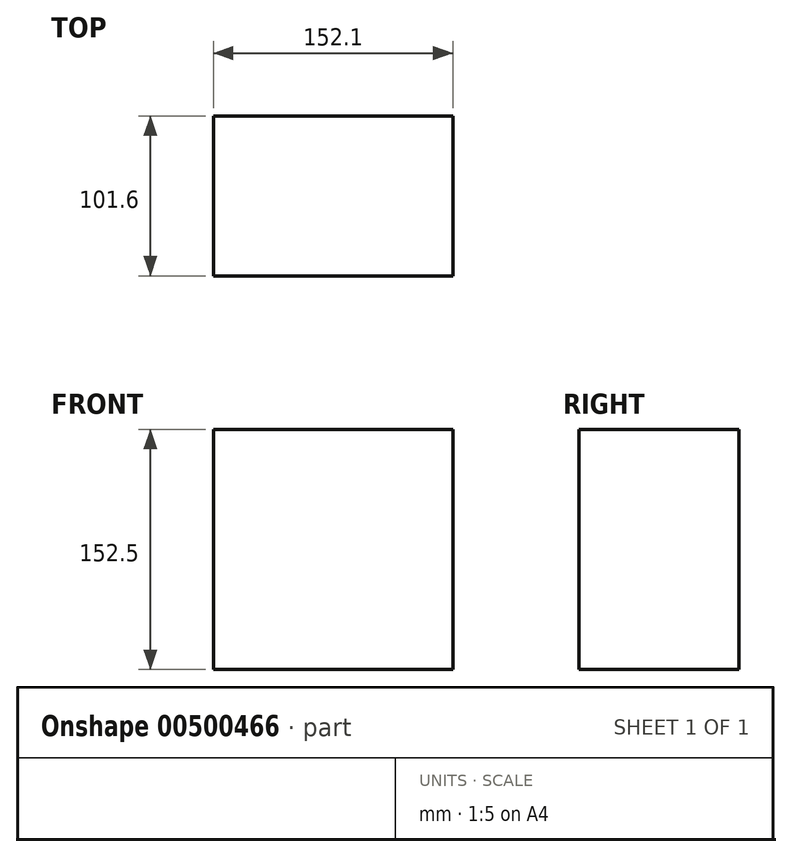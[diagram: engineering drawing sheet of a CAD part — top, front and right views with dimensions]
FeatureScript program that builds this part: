
annotation { "Feature Type Name" : "Feature", "Feature Type Description" : "" }
export const myFeature = defineFeature(function(context is Context, id is Id, definition is map)
    precondition{}
    {
        {
            var Q0;
            Q0=qCreatedBy(makeId("Front.planeOp"),FACE);
            var sketch = newSketch(context, id + "F0", { "sketchPlane" : qUnion([Q0])});
            skLineSegment(sketch, "E0", {"start": v(0, 0) * mm, "end": v(-75.85, 76.05) * mm});
            skLineSegment(sketch, "E1", {"start": v(0, 0) * mm, "end": v(76.25, 76.05) * mm});
            skLineSegment(sketch, "E2", {"start": v(76.25, 76.05) * mm, "end": v(0, 0) * mm});
            skLineSegment(sketch, "E3", {"start": v(0, 0) * mm, "end": v(76.25, -76.45) * mm});
            skLineSegment(sketch, "E4", {"start": v(76.25, -76.45) * mm, "end": v(0, 0) * mm});
            skLineSegment(sketch, "E5", {"start": v(0, 0) * mm, "end": v(-75.85, -76.45) * mm});
            skLineSegment(sketch, "E6", {"start": v(-75.85, -76.45) * mm, "end": v(0, 0) * mm});
            skLineSegment(sketch, "E7", {"start": v(-75.85, 76.05) * mm, "end": v(-75.85, -76.45) * mm});
            skLineSegment(sketch, "E8", {"start": v(-75.85, -76.45) * mm, "end": v(76.25, -76.45) * mm});
            skLineSegment(sketch, "E9", {"start": v(76.25, -76.45) * mm, "end": v(76.25, 76.05) * mm});
            skLineSegment(sketch, "E10", {"start": v(76.25, 76.05) * mm, "end": v(-75.85, 76.05) * mm});
            skSolve(sketch);
        }
        {
            var Q0;
            Q0 = qSketchRegion(id + "F0", true);
            extrude(context, id + "F1", {"entities" : qUnion([Q0]), "depth" : 101.6 * mm});
        }
    });
